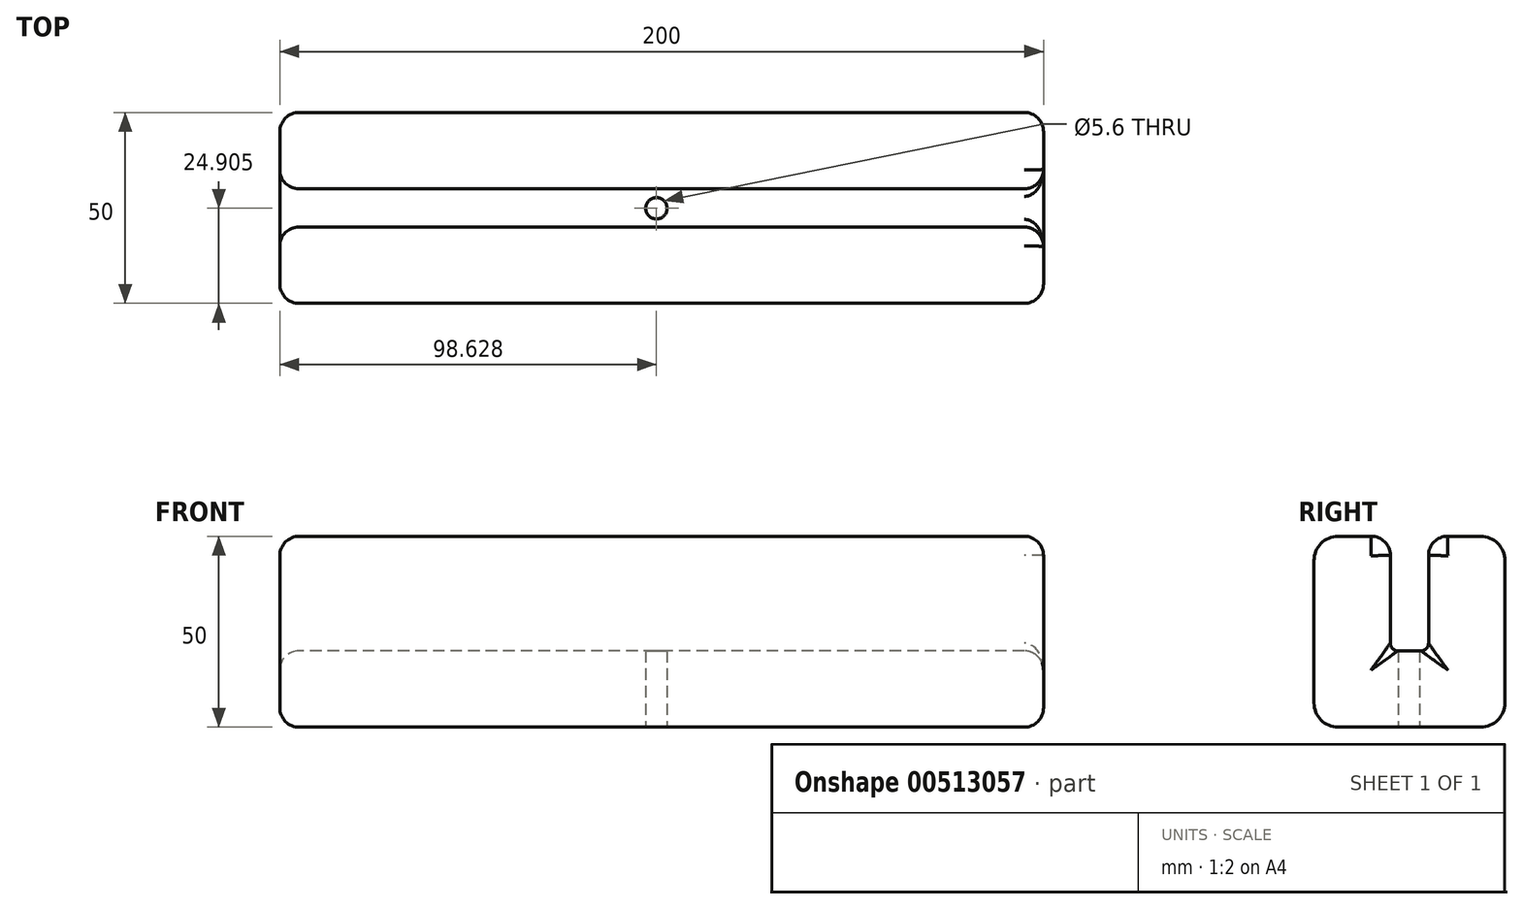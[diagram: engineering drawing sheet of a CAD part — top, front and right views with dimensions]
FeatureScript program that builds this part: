
annotation { "Feature Type Name" : "Feature", "Feature Type Description" : "" }
export const myFeature = defineFeature(function(context is Context, id is Id, definition is map)
    precondition{}
    {
        {
            var Q0;
            Q0=qCreatedBy(makeId("Right.planeOp"),FACE);
            var sketch = newSketch(context, id + "F0", { "sketchPlane" : qUnion([Q0])});
            skLineSegment(sketch, "E0", {"start": v(6.26, 50) * mm, "end": v(19.9, 50) * mm});
            skLineSegment(sketch, "E1", {"start": v(26.26, 43.65) * mm, "end": v(26.26, 6.35) * mm});
            skLineSegment(sketch, "E2", {"start": v(19.9, 0) * mm, "end": v(-17.4, 0) * mm});
            skLineSegment(sketch, "E3", {"start": v(-23.74, 6.35) * mm, "end": v(-23.74, 43.65) * mm});
            skLineSegment(sketch, "E4", {"start": v(-17.4, 50) * mm, "end": v(-3.74, 50) * mm});
            skLineSegment(sketch, "E5", {"start": v(-3.74, 50) * mm, "end": v(-3.74, 20) * mm});
            skLineSegment(sketch, "E6", {"start": v(-3.74, 20) * mm, "end": v(6.26, 20) * mm});
            skLineSegment(sketch, "E7", {"start": v(6.26, 20) * mm, "end": v(6.26, 50) * mm});
            skPoint(sketch, "E8.visualSharp", {"position": v(-23.74, 0) * mm});
            skArc(sketch, "E8.filletArc", {"start": v(-23.74, 6.35) * mm, "mid": v(-21.88, 1.86) * mm, "end": v(-17.4, 0) * mm});
            skPoint(sketch, "E9.visualSharp", {"position": v(26.26, 0) * mm});
            skArc(sketch, "E9.filletArc", {"start": v(19.9, 0) * mm, "mid": v(24.4, 1.86) * mm, "end": v(26.26, 6.35) * mm});
            skPoint(sketch, "E10.visualSharp", {"position": v(26.26, 50) * mm});
            skArc(sketch, "E10.filletArc", {"start": v(26.26, 43.65) * mm, "mid": v(24.4, 48.14) * mm, "end": v(19.9, 50) * mm});
            skPoint(sketch, "E11.visualSharp", {"position": v(-23.74, 50) * mm});
            skArc(sketch, "E11.filletArc", {"start": v(-17.4, 50) * mm, "mid": v(-21.88, 48.14) * mm, "end": v(-23.74, 43.65) * mm});
            skSolve(sketch);
        }
        {
            var Q0;
            Q0=makeQuery(id+"F0.imprint","IMPRINT",FACE,{"disambiguationData":[TD([[makeQuery(id+"F0.imprint","IMPRINT",EDGE,{"derivedFrom":sQuery(id+"F0.wireOp",EDGE,"E0")}),-1.0]])]});
            extrude(context, id + "F1", {"entities" : qUnion([Q0]), "depth" : 200 * mm, "offsetDistance" : 25 * mm});
        }
        {
            var Q0;
            Q0=makeQuery(id+"F1.opExtrude","CAP_FACE",FACE,{"disambiguationData":[OSD([sQuery(id+"F0.wireOp",EDGE,"E0"),sQuery(id+"F0.wireOp",EDGE,"E1"),sQuery(id+"F0.wireOp",EDGE,"E2"),sQuery(id+"F0.wireOp",EDGE,"E3"),sQuery(id+"F0.wireOp",EDGE,"E4"),sQuery(id+"F0.wireOp",EDGE,"E5"),sQuery(id+"F0.wireOp",EDGE,"E6"),sQuery(id+"F0.wireOp",EDGE,"E7"),sQuery(id+"F0.wireOp",EDGE,"E8.filletArc"),sQuery(id+"F0.wireOp",EDGE,"E9.filletArc"),sQuery(id+"F0.wireOp",EDGE,"E10.filletArc"),sQuery(id+"F0.wireOp",EDGE,"E11.filletArc")])],"isStart":false});
            var Q1;
            Q1=makeQuery(id+"F1.opExtrude","CAP_EDGE",EDGE,{"disambiguationData":[OSD([sQuery(id+"F0.wireOp",EDGE,"E2")])],"isStart":true});
            fillet(context, id + "F2", {"entities" : qUnion([Q0, Q1]), "radius" : 5.08 * mm, "tangentPropagation" : true, "allowEdgeOverflow" : false});
        }
        {
            var Q0;
            Q0=makeQuery(id+"F1.opExtrude","SWEPT_FACE",FACE,{"disambiguationData":[OSD([sQuery(id+"F0.wireOp",EDGE,"E2")])]});
            cPlane(context, id + "F3", {"entities" : qUnion([Q0]), "cplaneType" : CPlaneType.OFFSET, "offset" : 0 * mm, "width" : 152.4 * mm, "height" : 152.4 * mm});
        }
        {
            var Q0;
            Q0=qCreatedBy(id+"F3.planeOp",FACE);
            var sketch = newSketch(context, id + "F4", { "sketchPlane" : qUnion([Q0])});
            skCircle(sketch, "E12", {"center": v(98.63, -1.17) * mm, "radius": 2.8 * mm});
            skSolve(sketch);
        }
        {
            var Q0;
            Q0=makeQuery(id+"F1.opExtrude","SWEPT_EDGE",EDGE,{"disambiguationData":[OSD([sQuery(id+"F0.wireOp",EDGE,"E6"),sQuery(id+"F0.wireOp",EDGE,"E7")])]});
            var Q1;
            Q1=makeQuery(id+"F1.opExtrude","SWEPT_EDGE",EDGE,{"disambiguationData":[OSD([sQuery(id+"F0.wireOp",EDGE,"E5"),sQuery(id+"F0.wireOp",EDGE,"E6")])]});
            fillet(context, id + "F5", {"entities" : qUnion([Q0, Q1]), "radius" : 2 * mm, "tangentPropagation" : true, "allowEdgeOverflow" : false});
        }
        {
            var Q0;
            Q0=makeQuery(id+"F4.imprint","IMPRINT",FACE,{"disambiguationData":[TD([[makeQuery(id+"F4.imprint","IMPRINT",EDGE,{"derivedFrom":sQuery(id+"F4.wireOp",EDGE,"E12")}),1.0]])]});
            var Q1;
            Q1 = qConstructionFilter(qBodyType(qCreatedBy(id + "F4" ,EDGE), BodyType.WIRE), ConstructionObject.NO);
            extrude(context, id + "F6", {"entities" : qUnion([Q0]), "operationType" : NewBodyOperationType.REMOVE, "surfaceEntities" : qUnion([Q1]), "oppositeDirection" : true, "depth" : 20 * mm, "offsetDistance" : 25 * mm});
        }
        {
            var Q0;
            Q0=makeQuery(id+"F1.opExtrude","CAP_EDGE",EDGE,{"disambiguationData":[OSD([sQuery(id+"F0.wireOp",EDGE,"E7")])],"isStart":true});
            fillet(context, id + "F7", {"entities" : qUnion([Q0]), "radius" : 5 * mm, "tangentPropagation" : true, "allowEdgeOverflow" : false});
        }
    });
